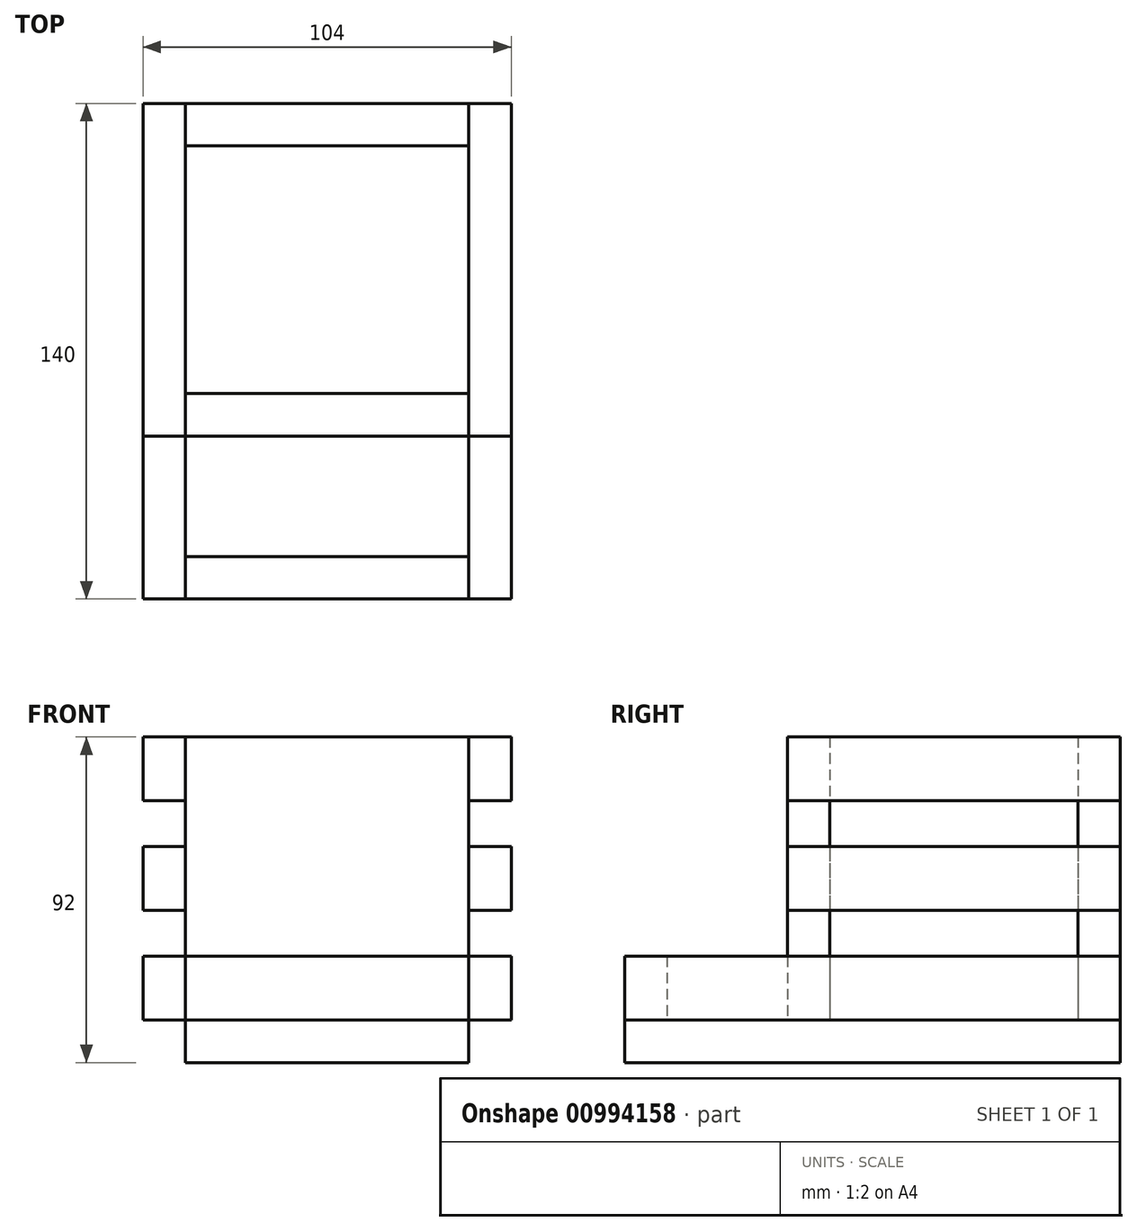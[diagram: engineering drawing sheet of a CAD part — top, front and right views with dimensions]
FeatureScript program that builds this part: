
annotation { "Feature Type Name" : "Feature", "Feature Type Description" : "" }
export const myFeature = defineFeature(function(context is Context, id is Id, definition is map)
    precondition{}
    {
        {
            var Q0;
            Q0=qCreatedBy(makeId("Top.planeOp"),FACE);
            var sketch = newSketch(context, id + "F0", { "sketchPlane" : qUnion([Q0])});
            skLineSegment(sketch, "E0.bottom", {"start": v(0, 0) * mm, "end": v(80, 0) * mm});
            skLineSegment(sketch, "E0.top", {"start": v(0, 140) * mm, "end": v(80, 140) * mm});
            skLineSegment(sketch, "E0.left", {"start": v(0, 0) * mm, "end": v(0, 140) * mm});
            skLineSegment(sketch, "E0.right", {"start": v(80, 0) * mm, "end": v(80, 140) * mm});
            skSolve(sketch);
        }
        {
            var Q0;
            Q0=makeQuery(id+"F0.imprint","IMPRINT",FACE,{"disambiguationData":[TD([[makeQuery(id+"F0.imprint","IMPRINT",EDGE,{"derivedFrom":sQuery(id+"F0.wireOp",EDGE,"E0.bottom")}),1.0]])]});
            extrude(context, id + "F1", {"entities" : qUnion([Q0]), "depth" : 12 * mm, "offsetDistance" : 25 * mm});
        }
        {
            var Q0;
            Q0=makeQuery(id+"F1.opExtrude","CAP_FACE",FACE,{"disambiguationData":[OSD([sQuery(id+"F0.wireOp",EDGE,"E0.bottom"),sQuery(id+"F0.wireOp",EDGE,"E0.top"),sQuery(id+"F0.wireOp",EDGE,"E0.left"),sQuery(id+"F0.wireOp",EDGE,"E0.right")])],"isStart":false});
            var sketch = newSketch(context, id + "F2", { "sketchPlane" : qUnion([Q0])});
            skLineSegment(sketch, "E1.bottom", {"start": v(0, 0) * mm, "end": v(80, 0) * mm});
            skLineSegment(sketch, "E1.top", {"start": v(0, 12) * mm, "end": v(80, 12) * mm});
            skLineSegment(sketch, "E1.left", {"start": v(0, 0) * mm, "end": v(0, 12) * mm});
            skLineSegment(sketch, "E2", {"start": v(80, 12) * mm, "end": v(80, 0) * mm});
            skLineSegment(sketch, "E3.bottom", {"start": v(0, 140) * mm, "end": v(80, 140) * mm});
            skLineSegment(sketch, "E3.top", {"start": v(0, 128) * mm, "end": v(80, 128) * mm});
            skLineSegment(sketch, "E3.left", {"start": v(0, 140) * mm, "end": v(0, 128) * mm});
            skLineSegment(sketch, "E3.right", {"start": v(80, 140) * mm, "end": v(80, 128) * mm});
            skLineSegment(sketch, "E4.bottom", {"start": v(0, 58) * mm, "end": v(80, 58) * mm});
            skLineSegment(sketch, "E4.top", {"start": v(0, 46) * mm, "end": v(80, 46) * mm});
            skLineSegment(sketch, "E4.left", {"start": v(0, 58) * mm, "end": v(0, 46) * mm});
            skLineSegment(sketch, "E4.right", {"start": v(80, 58) * mm, "end": v(80, 46) * mm});
            skSolve(sketch);
        }
        {
            var Q0;
            Q0=makeQuery(id+"F2.imprint","IMPRINT",FACE,{"disambiguationData":[TD([[makeQuery(id+"F2.imprint","IMPRINT",EDGE,{"derivedFrom":sQuery(id+"F2.wireOp",EDGE,"E3.bottom")}),-1.0]])]});
            var Q1;
            Q1=makeQuery(id+"F2.imprint","IMPRINT",FACE,{"disambiguationData":[TD([[makeQuery(id+"F2.imprint","IMPRINT",EDGE,{"derivedFrom":sQuery(id+"F2.wireOp",EDGE,"E4.bottom")}),-1.0]])]});
            extrude(context, id + "F3", {"entities" : qUnion([Q0, Q1]), "depth" : 80 * mm, "offsetDistance" : 25 * mm});
        }
        {
            var Q0;
            Q0=makeQuery(id+"F2.imprint","IMPRINT",FACE,{"disambiguationData":[TD([[makeQuery(id+"F2.imprint","IMPRINT",EDGE,{"derivedFrom":sQuery(id+"F2.wireOp",EDGE,"E1.bottom")}),1.0]])]});
            extrude(context, id + "F4", {"entities" : qUnion([Q0]), "depth" : 18 * mm, "offsetDistance" : 25 * mm});
        }
        {
            var Q0;
            Q0=makeQuery(id+"F4.opExtrude","SWEPT_FACE",FACE,{"disambiguationData":[OSD([sQuery(id+"F2.wireOp",EDGE,"E2")])]});
            var sketch = newSketch(context, id + "F5", { "sketchPlane" : qUnion([Q0])});
            skLineSegment(sketch, "E5.bottom", {"start": v(0, 30) * mm, "end": v(140, 30) * mm});
            skLineSegment(sketch, "E5.top", {"start": v(0, 12) * mm, "end": v(140, 12) * mm});
            skLineSegment(sketch, "E5.left", {"start": v(0, 30) * mm, "end": v(0, 12) * mm});
            skLineSegment(sketch, "E5.right", {"start": v(140, 30) * mm, "end": v(140, 12) * mm});
            skSolve(sketch);
        }
        {
            var Q0;
            {var subQ2=sQuery(id+"F5.wireOp",EDGE,"E5.right");Q0=makeQuery(id+"F5.imprint","IMPRINT",FACE,{"disambiguationData":[TD([[makeQuery(id+"F5.imprint","IMPRINT",EDGE,{"derivedFrom":subQ2}),-1.0]])]});}
            var Q1;
            {var subQ0=sQuery(id+"F5.wireOp",EDGE,"E5.left");Q1=makeQuery(id+"F5.imprint","IMPRINT",FACE,{"disambiguationData":[TD([[makeQuery(id+"F5.imprint","IMPRINT",EDGE,{"derivedFrom":subQ0}),1.0]])]});}
            extrude(context, id + "F6", {"entities" : qUnion([Q0, Q1]), "depth" : 12 * mm, "offsetDistance" : 25 * mm});
        }
        {
            var Q0;
            Q0=makeQuery(id+"F3.opExtrude","SWEPT_FACE",FACE,{"disambiguationData":[OSD([sQuery(id+"F2.wireOp",EDGE,"E4.right")])]});
            var sketch = newSketch(context, id + "F7", { "sketchPlane" : qUnion([Q0])});
            skLineSegment(sketch, "E6.bottom", {"start": v(46, 92) * mm, "end": v(140, 92) * mm});
            skLineSegment(sketch, "E6.top", {"start": v(46, 74) * mm, "end": v(140, 74) * mm});
            skLineSegment(sketch, "E6.left", {"start": v(46, 92) * mm, "end": v(46, 74) * mm});
            skLineSegment(sketch, "E6.right", {"start": v(140, 92) * mm, "end": v(140, 74) * mm});
            skLineSegment(sketch, "E7.bottom", {"start": v(46, 61) * mm, "end": v(140, 61) * mm});
            skLineSegment(sketch, "E7.top", {"start": v(46, 43) * mm, "end": v(140, 43) * mm});
            skLineSegment(sketch, "E7.left", {"start": v(46, 61) * mm, "end": v(46, 43) * mm});
            skLineSegment(sketch, "E7.right", {"start": v(140, 61) * mm, "end": v(140, 43) * mm});
            skSolve(sketch);
        }
        {
            var Q0;
            {var subQ3=sQuery(id+"F7.wireOp",EDGE,"E6.right");Q0=makeQuery(id+"F7.imprint","IMPRINT",FACE,{"disambiguationData":[TD([[makeQuery(id+"F7.imprint","IMPRINT",EDGE,{"derivedFrom":subQ3}),-1.0]])]});}
            var Q1;
            {var subQ5=sQuery(id+"F7.wireOp",EDGE,"E6.left");Q1=makeQuery(id+"F7.imprint","IMPRINT",FACE,{"disambiguationData":[TD([[makeQuery(id+"F7.imprint","IMPRINT",EDGE,{"derivedFrom":subQ5}),1.0]])]});}
            var Q2;
            {var subQ0=sQuery(id+"F7.wireOp",EDGE,"E7.left");Q2=makeQuery(id+"F7.imprint","IMPRINT",FACE,{"disambiguationData":[TD([[makeQuery(id+"F7.imprint","IMPRINT",EDGE,{"derivedFrom":subQ0}),1.0]])]});}
            var Q3;
            {var subQ0=sQuery(id+"F7.wireOp",EDGE,"E7.right");Q3=makeQuery(id+"F7.imprint","IMPRINT",FACE,{"disambiguationData":[TD([[makeQuery(id+"F7.imprint","IMPRINT",EDGE,{"derivedFrom":subQ0}),-1.0]])]});}
            extrude(context, id + "F8", {"entities" : qUnion([Q0, Q1, Q2, Q3]), "depth" : 12 * mm, "offsetDistance" : 25 * mm});
        }
        {
            var Q0;
            Q0=makeQuery(id+"F4.opExtrude","SWEPT_FACE",FACE,{"disambiguationData":[OSD([sQuery(id+"F2.wireOp",EDGE,"E1.left")])]});
            var sketch = newSketch(context, id + "F9", { "sketchPlane" : qUnion([Q0])});
            skLineSegment(sketch, "E8.bottom", {"start": v(0, 12) * mm, "end": v(-140, 12) * mm});
            skLineSegment(sketch, "E8.top", {"start": v(0, 30) * mm, "end": v(-140, 30) * mm});
            skLineSegment(sketch, "E8.left", {"start": v(0, 12) * mm, "end": v(0, 30) * mm});
            skLineSegment(sketch, "E8.right", {"start": v(-140, 12) * mm, "end": v(-140, 30) * mm});
            skSolve(sketch);
        }
        {
            var Q0;
            Q0=makeQuery(id+"F3.opExtrude","SWEPT_FACE",FACE,{"disambiguationData":[OSD([sQuery(id+"F2.wireOp",EDGE,"E4.left")])]});
            var sketch = newSketch(context, id + "F10", { "sketchPlane" : qUnion([Q0])});
            skLineSegment(sketch, "E9.bottom", {"start": v(-46, 92) * mm, "end": v(-140, 92) * mm});
            skLineSegment(sketch, "E9.top", {"start": v(-46, 74) * mm, "end": v(-140, 74) * mm});
            skLineSegment(sketch, "E9.left", {"start": v(-46, 92) * mm, "end": v(-46, 74) * mm});
            skLineSegment(sketch, "E9.right", {"start": v(-140, 92) * mm, "end": v(-140, 74) * mm});
            skLineSegment(sketch, "E10.bottom", {"start": v(-46, 61) * mm, "end": v(-140, 61) * mm});
            skLineSegment(sketch, "E10.top", {"start": v(-46, 43) * mm, "end": v(-140, 43) * mm});
            skLineSegment(sketch, "E10.left", {"start": v(-46, 61) * mm, "end": v(-46, 43) * mm});
            skLineSegment(sketch, "E10.right", {"start": v(-140, 61) * mm, "end": v(-140, 43) * mm});
            skSolve(sketch);
        }
        {
            var Q0;
            {var subQ5=sQuery(id+"F10.wireOp",EDGE,"E9.left");Q0=makeQuery(id+"F10.imprint","IMPRINT",FACE,{"disambiguationData":[TD([[makeQuery(id+"F10.imprint","IMPRINT",EDGE,{"derivedFrom":subQ5}),-1.0]])]});}
            var Q1;
            {var subQ3=sQuery(id+"F10.wireOp",EDGE,"E9.right");Q1=makeQuery(id+"F10.imprint","IMPRINT",FACE,{"disambiguationData":[TD([[makeQuery(id+"F10.imprint","IMPRINT",EDGE,{"derivedFrom":subQ3}),1.0]])]});}
            var Q2;
            {var subQ0=sQuery(id+"F10.wireOp",EDGE,"E10.left");Q2=makeQuery(id+"F10.imprint","IMPRINT",FACE,{"disambiguationData":[TD([[makeQuery(id+"F10.imprint","IMPRINT",EDGE,{"derivedFrom":subQ0}),-1.0]])]});}
            var Q3;
            {var subQ0=sQuery(id+"F10.wireOp",EDGE,"E10.right");Q3=makeQuery(id+"F10.imprint","IMPRINT",FACE,{"disambiguationData":[TD([[makeQuery(id+"F10.imprint","IMPRINT",EDGE,{"derivedFrom":subQ0}),1.0]])]});}
            var Q4;
            {var subQ0=sQuery(id+"F9.wireOp",EDGE,"E8.left");Q4=makeQuery(id+"F9.imprint","IMPRINT",FACE,{"disambiguationData":[TD([[makeQuery(id+"F9.imprint","IMPRINT",EDGE,{"derivedFrom":subQ0}),-1.0]])]});}
            var Q5;
            {var subQ2=sQuery(id+"F9.wireOp",EDGE,"E8.right");Q5=makeQuery(id+"F9.imprint","IMPRINT",FACE,{"disambiguationData":[TD([[makeQuery(id+"F9.imprint","IMPRINT",EDGE,{"derivedFrom":subQ2}),-1.0]])]});}
            extrude(context, id + "F11", {"entities" : qUnion([Q0, Q1, Q2, Q3, Q4, Q5]), "depth" : 12 * mm, "offsetDistance" : 25 * mm});
        }
    });
